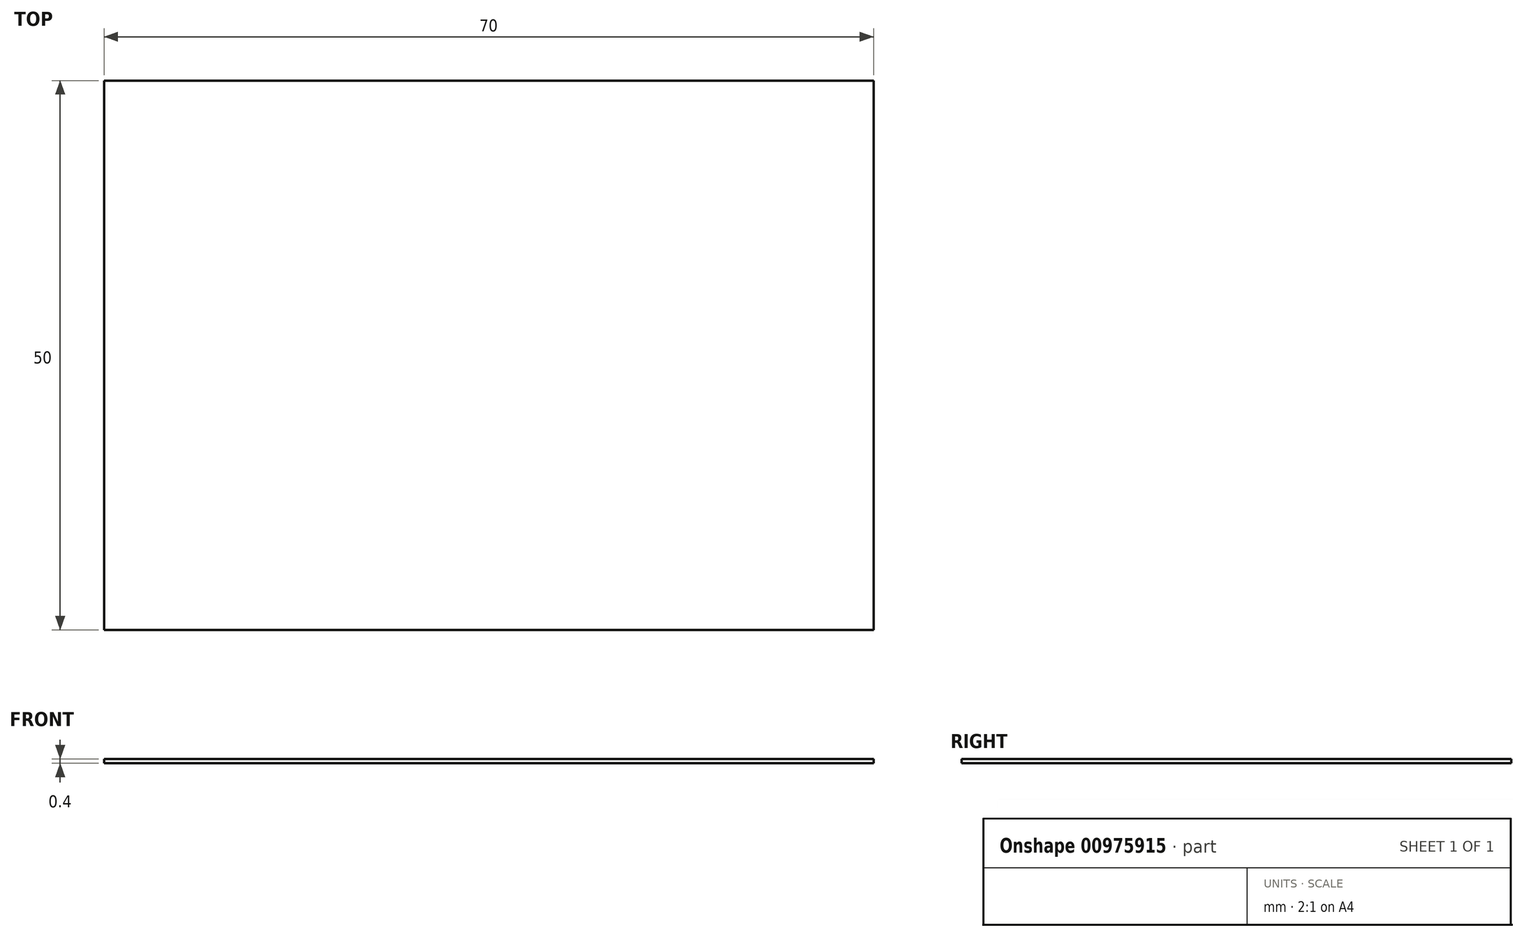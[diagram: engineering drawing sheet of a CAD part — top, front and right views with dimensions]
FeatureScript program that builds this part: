
annotation { "Feature Type Name" : "Feature", "Feature Type Description" : "" }
export const myFeature = defineFeature(function(context is Context, id is Id, definition is map)
    precondition{}
    {
        {
            var Q0;
            Q0=qCreatedBy(makeId("Top.planeOp"),FACE);
            var sketch = newSketch(context, id + "F0", { "sketchPlane" : qUnion([Q0])});
            skLineSegment(sketch, "E0.bottom", {"start": v(-35, 25) * mm, "end": v(35, 25) * mm});
            skLineSegment(sketch, "E0.top", {"start": v(-35, -25) * mm, "end": v(35, -25) * mm});
            skLineSegment(sketch, "E0.left", {"start": v(-35, 25) * mm, "end": v(-35, -25) * mm});
            skLineSegment(sketch, "E0.right", {"start": v(35, 25) * mm, "end": v(35, -25) * mm});
            skPoint(sketch, "E0.middle", {"position": v(0, 0) * mm});
            skSolve(sketch);
        }
        {
            var Q0;
            Q0=makeQuery(id+"F0.imprint","IMPRINT",FACE,{"disambiguationData":[TD([[makeQuery(id+"F0.imprint","IMPRINT",EDGE,{"derivedFrom":sQuery(id+"F0.wireOp",EDGE,"E0.bottom")}),-1.0]])]});
            extrude(context, id + "F1", {"entities" : qUnion([Q0]), "depth" : 0.4 * mm, "offsetDistance" : 25 * mm});
        }
    });
